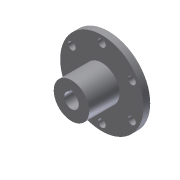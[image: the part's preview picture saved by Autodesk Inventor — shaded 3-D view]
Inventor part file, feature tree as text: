
AUTODESK INVENTOR PART (.ipt)
format: ipt  version: 2013 (Build 170138000, 138)  size: 119,296 bytes
history: native  units: in
note: dims shown in document units (in); Inventor stores cm internally (conversion verified against a paired STEP export)
features: extrude x4, sketch x4, pattern_circular x1, projected_geometry x1
ambient origin geometry x8: Origin, YZ Plane, XZ Plane, XY Plane, X Axis, Y Axis, Z Axis, Center Point
bodies: Solid1 (feature_tree)
feature tree (10):
  extrude  "Extrusion1"  Depth=0.18in TaperAngle=0.0deg
  extrude  "Extrusion2"  Depth=0.82in TaperAngle=0.0deg
  extrude  "Extrusion3"  Depth=0.0984in
  extrude  "Extrusion4"  Depth=0.82in TaperAngle=0.0deg
  pattern_circular  "Circular Pattern1"  [2 undecoded]
  sketch  "Sketch1"  dims[d0=2.25in d1=0.18in d2=0.0in]
  sketch  "Sketch2"  dims[d3=0.958in d4=0.82in d5=0.0in]
  sketch  "Sketch3"  dims[d6=0.3937in d7=0.0984in]
  sketch  "Sketch4"  dims[d8=0.0984in d9=0.82in d10=0.0in d11=0.206in d12=0.9375in d13=1.0in d14=0.0in d15=2.3622in d16=360.0deg]
  projected_geometry  "Projected Loop1"
note: 2 required parameter values undecoded (feature->parameter linkage not recoverable at this tier; creation-order binding heuristic only, values carry confidence <= 0.55)
